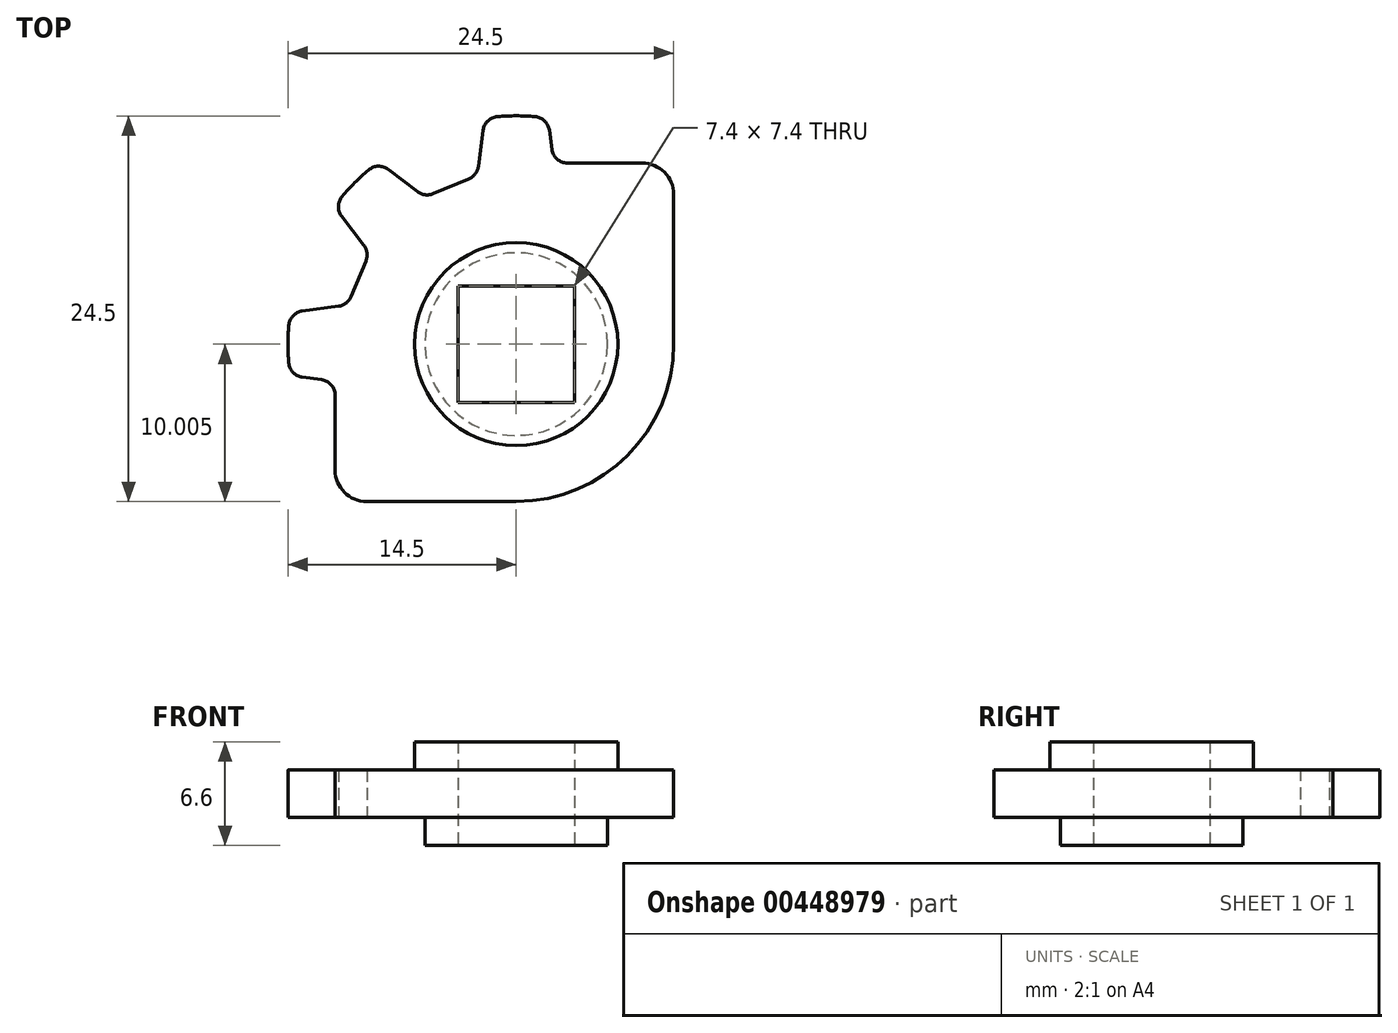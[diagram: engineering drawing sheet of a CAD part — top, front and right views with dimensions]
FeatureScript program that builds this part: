
annotation { "Feature Type Name" : "Feature", "Feature Type Description" : "" }
export const myFeature = defineFeature(function(context is Context, id is Id, definition is map)
    precondition{}
    {
        {
            var Q0;
            Q0=qCreatedBy(makeId("Top.planeOp"),FACE);
            var sketch = newSketch(context, id + "F0", { "sketchPlane" : qUnion([Q0])});
            skCircle(sketch, "E0", {"center": v(-11.81, -3.65) * mm, "radius": 6.5 * mm});
            skPoint(sketch, "E0.first.point", {"position": v(-16.63, -8) * mm});
            skPoint(sketch, "E0.second.point", {"position": v(-6.66, -7.61) * mm});
            skPoint(sketch, "E0.third.point", {"position": v(-6.94, 0.66) * mm});
            skArc(sketch, "E1", {"start": v(-11.81, -13.65) * mm, "mid": v(-4.74, -10.72) * mm, "end": v(-1.81, -3.65) * mm});
            skLineSegment(sketch, "E2", {"start": v(-22.81, -13.65) * mm, "end": v(-11.81, -13.65) * mm});
            skLineSegment(sketch, "E3", {"start": v(-1.81, -3.65) * mm, "end": v(-1.81, 7.35) * mm});
            skLineSegment(sketch, "E4", {"start": v(-11.81, -3.65) * mm, "end": v(-28.26, 12.8) * mm, "construction": true});
            skArc(sketch, "E5", {"start": v(-26.17, -1.65) * mm, "mid": v(-26.31, -3.65) * mm, "end": v(-26.17, -5.64) * mm});
            skLineSegment(sketch, "E6.bottom", {"start": v(-8.11, 0.05) * mm, "end": v(-15.51, 0.05) * mm});
            skLineSegment(sketch, "E6.top", {"start": v(-8.11, -7.35) * mm, "end": v(-15.51, -7.35) * mm});
            skLineSegment(sketch, "E6.left", {"start": v(-8.11, 0.05) * mm, "end": v(-8.11, -7.35) * mm});
            skLineSegment(sketch, "E6.right", {"start": v(-15.51, 0.05) * mm, "end": v(-15.51, -7.35) * mm});
            skLineSegment(sketch, "E7", {"start": v(-23.38, 5.1) * mm, "end": v(-21.14, 2.18) * mm});
            skPoint(sketch, "E8", {"position": v(-19.59, 4.13) * mm});
            skPoint(sketch, "E9", {"position": v(-22.06, 6.6) * mm});
            skLineSegment(sketch, "E10", {"start": v(-20.55, 7.92) * mm, "end": v(-17.63, 5.69) * mm});
            skLineSegment(sketch, "E11", {"start": v(-11.81, -3.65) * mm, "end": v(-11.81, 17) * mm, "construction": true});
            skLineSegment(sketch, "E12", {"start": v(-11.81, -3.65) * mm, "end": v(-30.33, -3.65) * mm, "construction": true});
            skLineSegment(sketch, "E13", {"start": v(-14.3, 7.07) * mm, "end": v(-13.8, 10.72) * mm});
            skLineSegment(sketch, "E14", {"start": v(-9.43, 7.85) * mm, "end": v(-9.81, 10.72) * mm});
            skPoint(sketch, "E15", {"position": v(-11.81, 10.85) * mm});
            skPoint(sketch, "E16", {"position": v(-11.81, 7.35) * mm});
            skLineSegment(sketch, "E17", {"start": v(-26.17, -1.65) * mm, "end": v(-22.53, -1.16) * mm});
            skLineSegment(sketch, "E18", {"start": v(-26.17, -5.64) * mm, "end": v(-23.31, -6.02) * mm});
            skPoint(sketch, "E19", {"position": v(-26.31, -3.65) * mm});
            skPoint(sketch, "E20", {"position": v(-22.81, -3.65) * mm});
            skArc(sketch, "E21.trimOffspring", {"start": v(-20.55, 7.92) * mm, "mid": v(-22.06, 6.6) * mm, "end": v(-23.38, 5.1) * mm});
            skArc(sketch, "E22.trimOffspring", {"start": v(-9.81, 10.72) * mm, "mid": v(-11.81, 10.85) * mm, "end": v(-13.8, 10.72) * mm});
            skLineSegment(sketch, "E23", {"start": v(-22.53, -1.16) * mm, "end": v(-21.14, 2.18) * mm});
            skLineSegment(sketch, "E24", {"start": v(-17.63, 5.69) * mm, "end": v(-14.3, 7.07) * mm});
            skLineSegment(sketch, "E25", {"start": v(-22.81, -13.65) * mm, "end": v(-23.31, -13.65) * mm});
            skLineSegment(sketch, "E26", {"start": v(-23.31, -13.65) * mm, "end": v(-23.31, -6.02) * mm});
            skLineSegment(sketch, "E27", {"start": v(-1.81, 7.35) * mm, "end": v(-1.81, 7.85) * mm});
            skLineSegment(sketch, "E28", {"start": v(-1.81, 7.85) * mm, "end": v(-9.43, 7.85) * mm});
            skPoint(sketch, "E29.orphan", {"position": v(-22.53, -6.13) * mm});
            skPoint(sketch, "E30.orphan", {"position": v(-9.33, 7.07) * mm});
            skCircle(sketch, "E31", {"center": v(-11.81, -3.65) * mm, "radius": 5.8 * mm});
            skSolve(sketch);
        }
        {
            var Q0;
            Q0=makeQuery(id+"F0.imprint","IMPRINT",FACE,{"disambiguationData":[TD([[makeQuery(id+"F0.imprint","IMPRINT",EDGE,{"derivedFrom":sQuery(id+"F0.wireOp",EDGE,"E6.bottom")}),-1.0]])]});
            extrude(context, id + "F1", {"entities" : qUnion([Q0]), "endBound" : BoundingType.SYMMETRIC, "depth" : (3 + 1.8 + 1.8) * mm});
        }
        {
            var Q0;
            Q0=makeQuery(id+"F0.imprint","IMPRINT",FACE,{"disambiguationData":[TD([[makeQuery(id+"F0.imprint","IMPRINT",EDGE,{"derivedFrom":sQuery(id+"F0.wireOp",EDGE,"E0")}),-1.0]])]});
            var Q1;
            Q1=makeQuery(id+"F0.imprint","IMPRINT",FACE,{"disambiguationData":[TD([[makeQuery(id+"F0.imprint","IMPRINT",EDGE,{"derivedFrom":sQuery(id+"F0.wireOp",EDGE,"E0")}),1.0]])]});
            extrude(context, id + "F2", {"entities" : qUnion([Q0, Q1]), "operationType" : NewBodyOperationType.ADD, "endBound" : BoundingType.SYMMETRIC, "depth" : 3 * mm});
        }
        {
            var Q0;
            Q0=makeQuery(id+"F2.opExtrude","SWEPT_EDGE",EDGE,{"disambiguationData":[OSD([sQuery(id+"F0.wireOp",EDGE,"E25"),sQuery(id+"F0.wireOp",EDGE,"E26")])]});
            var Q1;
            Q1=makeQuery(id+"F2.opExtrude","SWEPT_EDGE",EDGE,{"disambiguationData":[OSD([sQuery(id+"F0.wireOp",EDGE,"E27"),sQuery(id+"F0.wireOp",EDGE,"E28")])]});
            fillet(context, id + "F3", {"entities" : qUnion([Q0, Q1]), "radius" : 2 * mm, "tangentPropagation" : true, "allowEdgeOverflow" : false});
        }
        {
            var Q0;
            Q0=makeQuery(id+"F2.opExtrude","SWEPT_EDGE",EDGE,{"disambiguationData":[OSD([sQuery(id+"F0.wireOp",EDGE,"E5"),sQuery(id+"F0.wireOp",EDGE,"E18")])]});
            var Q1;
            Q1=makeQuery(id+"F2.opExtrude","SWEPT_EDGE",EDGE,{"disambiguationData":[OSD([sQuery(id+"F0.wireOp",EDGE,"E5"),sQuery(id+"F0.wireOp",EDGE,"E17")])]});
            var Q2;
            Q2=makeQuery(id+"F2.opExtrude","SWEPT_EDGE",EDGE,{"disambiguationData":[OSD([sQuery(id+"F0.wireOp",EDGE,"E7"),sQuery(id+"F0.wireOp",EDGE,"E21.trimOffspring")])]});
            var Q3;
            Q3=makeQuery(id+"F2.opExtrude","SWEPT_EDGE",EDGE,{"disambiguationData":[OSD([sQuery(id+"F0.wireOp",EDGE,"E10"),sQuery(id+"F0.wireOp",EDGE,"E21.trimOffspring")])]});
            var Q4;
            Q4=makeQuery(id+"F2.opExtrude","SWEPT_EDGE",EDGE,{"disambiguationData":[OSD([sQuery(id+"F0.wireOp",EDGE,"E13"),sQuery(id+"F0.wireOp",EDGE,"E22.trimOffspring")])]});
            var Q5;
            Q5=makeQuery(id+"F2.opExtrude","SWEPT_EDGE",EDGE,{"disambiguationData":[OSD([sQuery(id+"F0.wireOp",EDGE,"E14"),sQuery(id+"F0.wireOp",EDGE,"E22.trimOffspring")])]});
            fillet(context, id + "F4", {"entities" : qUnion([Q0, Q1, Q2, Q3, Q4, Q5]), "radius" : 1 * mm, "tangentPropagation" : true, "allowEdgeOverflow" : false});
        }
        {
            var Q0;
            Q0=makeQuery(id+"F2.opExtrude","SWEPT_EDGE",EDGE,{"disambiguationData":[OSD([sQuery(id+"F0.wireOp",EDGE,"E18"),sQuery(id+"F0.wireOp",EDGE,"E26")])]});
            var Q1;
            Q1=makeQuery(id+"F2.opExtrude","SWEPT_EDGE",EDGE,{"disambiguationData":[OSD([sQuery(id+"F0.wireOp",EDGE,"E17"),sQuery(id+"F0.wireOp",EDGE,"E23")])]});
            var Q2;
            Q2=makeQuery(id+"F2.opExtrude","SWEPT_EDGE",EDGE,{"disambiguationData":[OSD([sQuery(id+"F0.wireOp",EDGE,"E7"),sQuery(id+"F0.wireOp",EDGE,"E23")])]});
            var Q3;
            Q3=makeQuery(id+"F2.opExtrude","SWEPT_EDGE",EDGE,{"disambiguationData":[OSD([sQuery(id+"F0.wireOp",EDGE,"E10"),sQuery(id+"F0.wireOp",EDGE,"E24")])]});
            var Q4;
            Q4=makeQuery(id+"F2.opExtrude","SWEPT_EDGE",EDGE,{"disambiguationData":[OSD([sQuery(id+"F0.wireOp",EDGE,"E13"),sQuery(id+"F0.wireOp",EDGE,"E24")])]});
            var Q5;
            Q5=makeQuery(id+"F2.opExtrude","SWEPT_EDGE",EDGE,{"disambiguationData":[OSD([sQuery(id+"F0.wireOp",EDGE,"E14"),sQuery(id+"F0.wireOp",EDGE,"E28")])]});
            fillet(context, id + "F5", {"entities" : qUnion([Q0, Q1, Q2, Q3, Q4, Q5]), "radius" : 1 * mm, "tangentPropagation" : true, "allowEdgeOverflow" : false});
        }
        {
            var Q0;
            Q0=makeQuery(id+"F2.opExtrude","CAP_FACE",FACE,{"disambiguationData":[OSD([sQuery(id+"F0.wireOp",EDGE,"E1"),sQuery(id+"F0.wireOp",EDGE,"E2"),sQuery(id+"F0.wireOp",EDGE,"E3"),sQuery(id+"F0.wireOp",EDGE,"E5"),sQuery(id+"F0.wireOp",EDGE,"E7"),sQuery(id+"F0.wireOp",EDGE,"E10"),sQuery(id+"F0.wireOp",EDGE,"E13"),sQuery(id+"F0.wireOp",EDGE,"E14"),sQuery(id+"F0.wireOp",EDGE,"E17"),sQuery(id+"F0.wireOp",EDGE,"E18"),sQuery(id+"F0.wireOp",EDGE,"E21.trimOffspring"),sQuery(id+"F0.wireOp",EDGE,"E22.trimOffspring"),sQuery(id+"F0.wireOp",EDGE,"E23"),sQuery(id+"F0.wireOp",EDGE,"E24"),sQuery(id+"F0.wireOp",EDGE,"E25"),sQuery(id+"F0.wireOp",EDGE,"E26"),sQuery(id+"F0.wireOp",EDGE,"E27"),sQuery(id+"F0.wireOp",EDGE,"E28"),sQuery(id+"F0.wireOp",EDGE,"E31")])],"isStart":false});
            var sketch = newSketch(context, id + "F6", { "sketchPlane" : qUnion([Q0])});
            skCircle(sketch, "E32", {"center": v(-11.81, -3.65) * mm, "radius": 6.45 * mm});
            skSolve(sketch);
        }
        {
            var Q0;
            Q0=makeQuery(id+"F6.imprint","IMPRINT",FACE,{"disambiguationData":[TD([[makeQuery(id+"F6.imprint","IMPRINT",EDGE,{"derivedFrom":sQuery(id+"F6.wireOp",EDGE,"E32")}),1.0]])]});
            var Q1;
            Q1=makeQuery(id+"F1.opExtrude","CAP_FACE",FACE,{"disambiguationData":[OSD([sQuery(id+"F0.wireOp",EDGE,"E6.bottom"),sQuery(id+"F0.wireOp",EDGE,"E6.top"),sQuery(id+"F0.wireOp",EDGE,"E6.left"),sQuery(id+"F0.wireOp",EDGE,"E6.right"),sQuery(id+"F0.wireOp",EDGE,"E31")])],"isStart":false});
            extrude(context, id + "F7", {"entities" : qUnion([Q0]), "operationType" : NewBodyOperationType.ADD, "endBound" : BoundingType.UP_TO_SURFACE, "endBoundEntityFace" : qUnion([Q1]), "depth" : 25 * mm});
        }
    });
